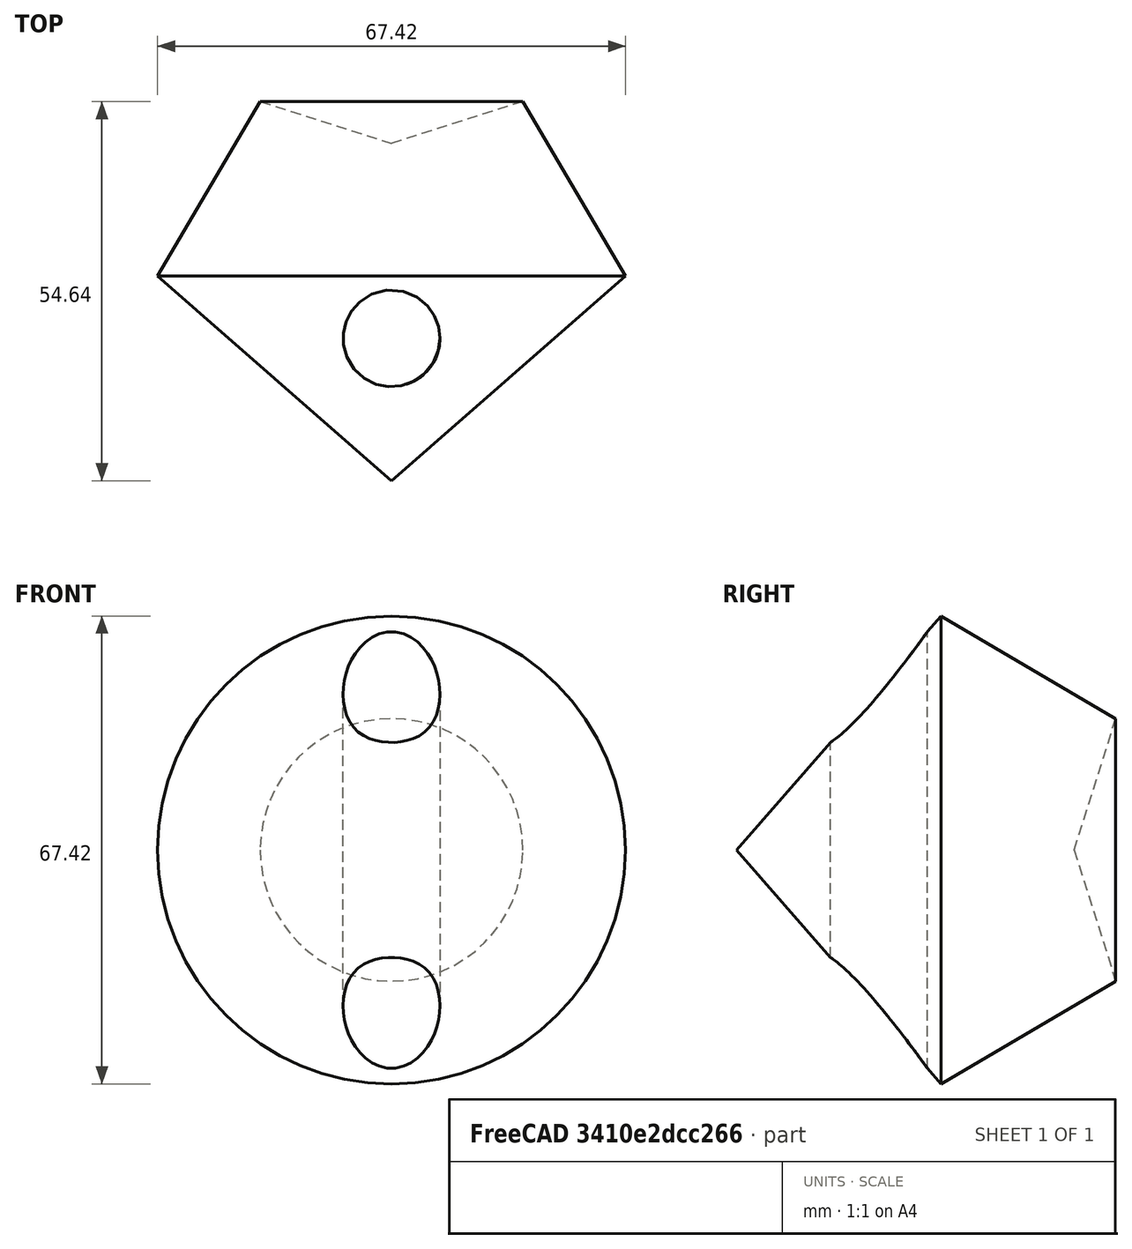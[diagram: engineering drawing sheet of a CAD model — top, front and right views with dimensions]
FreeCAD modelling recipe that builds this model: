
FCSTD DOCUMENT  (FreeCAD 0.16R6707 (Git))
Label: fusée
License: All rights reserved
LicenseURL: http://en.wikipedia.org/wiki/All_rights_reserved
objects: Sketcher::SketchObject×2, PartDesign::Revolution×1, PartDesign::Pocket×1, PartDesign::Mirrored×1
note: 7 computed .brp shape members not serialized (recipe doc carries the construction recipe); baked Part::Feature solids carry a one-line shape summary decoded from their .brp

FEATURE [Sketcher::SketchObject] Sketch
  sketch-geometry (4):
    g0: LineSegment StartX=0 StartY=0 StartZ=0 EndX=33.7135 EndY=29.4861 EndZ=0
    g1: LineSegment StartX=33.7135 StartY=29.4861 StartZ=0 EndX=18.9176 EndY=54.6391 EndZ=0
    g2: LineSegment StartX=18.9176 StartY=54.6391 StartZ=0 EndX=0 EndY=48.6573 EndZ=0
    g3: LineSegment StartX=0 StartY=48.6573 StartZ=0 EndX=0 EndY=0 EndZ=0
  constraints (6):
    c: Coincident(g-1,g0)
    c: Coincident(g0,g1)
    c: Coincident(g1,g2)
    c: PointOnObject(g2,g-2)
    c: Coincident(g2,g3)
    c: Coincident(g3,g0)
FEATURE [PartDesign::Revolution] Revolution
  Angle = 180
  Axis = (0,1,0)
  Base = (0,0,0)
  ReferenceAxis = -> Sketch [V_Axis]
  Reversed = true
  Sketch = -> Sketch
FEATURE [Sketcher::SketchObject] Sketch001
  Placement = pos=(0,0,0) rot=(1,0,0;3.14159rad)
  Support = -> Revolution [Face5]
  sketch-geometry (1):
    g0: Circle CenterX=0 CenterY=-20.5369 CenterZ=0 NormalX=0 NormalY=0 NormalZ=1 Radius=6.98006
  constraints (1):
    c: PointOnObject(g0,g-2)
FEATURE [PartDesign::Pocket] Pocket
  Length = 5
  Midplane = true
  Sketch = -> Sketch001
  Type = 1
FEATURE [PartDesign::Mirrored] Mirrored
  MirrorPlane = -> Revolution [Face5]
  Originals = -> [Revolution,Pocket]
